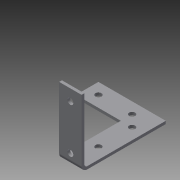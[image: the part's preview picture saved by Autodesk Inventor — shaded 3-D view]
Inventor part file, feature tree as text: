
AUTODESK INVENTOR PART (.ipt)
format: ipt  version: 2013 (Build 170138000, 138)  size: 128,000 bytes
history: native  units: in
note: dims shown in document units (in); Inventor stores cm internally (conversion verified against a paired STEP export)
features: sheet_metal_op x4, sketch x3, other x3
ambient origin geometry x8: Origin, YZ Plane, XZ Plane, XY Plane, X Axis, Y Axis, Z Axis, Center Point
bodies: Solid1 (feature_tree)
feature tree (10):
  sheet_metal_op  "Face1"
  sheet_metal_op  "Flange1"
  sketch  "Sketch1"  dims[d0=3.0in d1=1.0in d2=2.0in d3=2.0in d4=1.0in d5=0.266in d6=0.266in d7=0.266in d8=0.266in d9=0.5in d10=0.0in d11=0.5in d12=0.5in d13=0.5in d15=0.5in]
  other  "Plate1"
  sketch  "Sketch2"  dims[d17=0.75in]
  other  "Plate2"
  sheet_metal_op  "Bend1"
  sheet_metal_op  "Corner1"
  sketch  "Sketch3"  dims[d18=0.125in d19=0.125in d20=0.0625in d21=0.25in d22=0.125in d23=3.0in d24=90.0deg d25=0.125in d26=0.5in d27=0.125in d28=0.125in d29=0.266in d30=0.266in d31=0.5in d32=2.0in d33=0.125in d34=0.0in]
  other  "Cut1"
